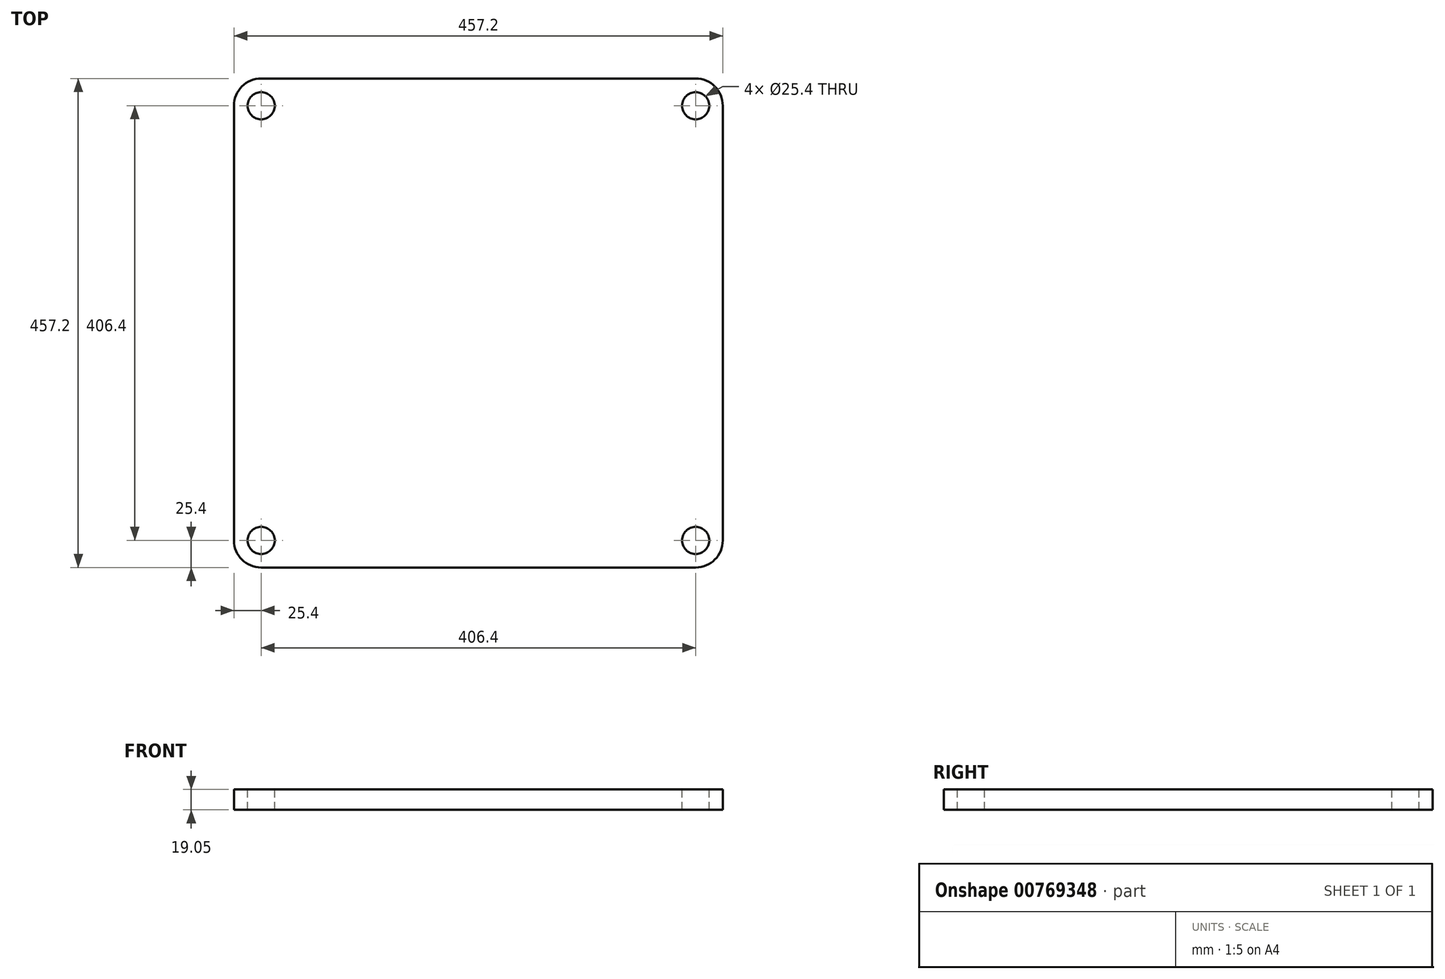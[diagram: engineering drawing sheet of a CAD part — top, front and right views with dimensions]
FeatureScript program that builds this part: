
annotation { "Feature Type Name" : "Feature", "Feature Type Description" : "" }
export const myFeature = defineFeature(function(context is Context, id is Id, definition is map)
    precondition{}
    {
        {
            var Q0;
            Q0=qCreatedBy(makeId("Top.planeOp"),FACE);
            var sketch = newSketch(context, id + "F0", { "sketchPlane" : qUnion([Q0])});
            skLineSegment(sketch, "E0.bottom", {"start": v(228.6, 228.6) * mm, "end": v(-228.6, 228.6) * mm});
            skLineSegment(sketch, "E0.top", {"start": v(228.6, -228.6) * mm, "end": v(-228.6, -228.6) * mm});
            skLineSegment(sketch, "E0.left", {"start": v(228.6, 228.6) * mm, "end": v(228.6, -228.6) * mm});
            skLineSegment(sketch, "E0.right", {"start": v(-228.6, 228.6) * mm, "end": v(-228.6, -228.6) * mm});
            skPoint(sketch, "E0.middle", {"position": v(0, 0) * mm});
            skSolve(sketch);
        }
        {
            var Q0;
            Q0=makeQuery(id+"F0.imprint","IMPRINT",FACE,{"disambiguationData":[TD([[makeQuery(id+"F0.imprint","IMPRINT",EDGE,{"derivedFrom":sQuery(id+"F0.wireOp",EDGE,"E0.bottom")}),1.0]])]});
            extrude(context, id + "F1", {"entities" : qUnion([Q0]), "depth" : 19.05 * mm, "offsetDistance" : 25.4 * mm});
        }
        {
            var Q0;
            Q0=makeQuery(id+"F1.opExtrude","SWEPT_EDGE",EDGE,{"disambiguationData":[OSD([sQuery(id+"F0.wireOp",EDGE,"E0.top"),sQuery(id+"F0.wireOp",EDGE,"E0.left")])]});
            var Q1;
            Q1=makeQuery(id+"F1.opExtrude","SWEPT_EDGE",EDGE,{"disambiguationData":[OSD([sQuery(id+"F0.wireOp",EDGE,"E0.bottom"),sQuery(id+"F0.wireOp",EDGE,"E0.left")])]});
            var Q2;
            Q2=makeQuery(id+"F1.opExtrude","SWEPT_EDGE",EDGE,{"disambiguationData":[OSD([sQuery(id+"F0.wireOp",EDGE,"E0.top"),sQuery(id+"F0.wireOp",EDGE,"E0.right")])]});
            var Q3;
            Q3=makeQuery(id+"F1.opExtrude","SWEPT_EDGE",EDGE,{"disambiguationData":[OSD([sQuery(id+"F0.wireOp",EDGE,"E0.bottom"),sQuery(id+"F0.wireOp",EDGE,"E0.right")])]});
            fillet(context, id + "F2", {"entities" : qUnion([Q0, Q1, Q2, Q3]), "radius" : 25.4 * mm, "tangentPropagation" : true, "allowEdgeOverflow" : false});
        }
        {
            var Q0;
            Q0=makeQuery(id+"F1.opExtrude","CAP_FACE",FACE,{"disambiguationData":[OSD([sQuery(id+"F0.wireOp",EDGE,"E0.bottom"),sQuery(id+"F0.wireOp",EDGE,"E0.top"),sQuery(id+"F0.wireOp",EDGE,"E0.left"),sQuery(id+"F0.wireOp",EDGE,"E0.right")])],"isStart":false});
            var sketch = newSketch(context, id + "F3", { "sketchPlane" : qUnion([Q0])});
            skArc(sketch, "E1.0", {"start": v(-203.2, 228.6) * mm, "mid": v(-221.16, 221.16) * mm, "end": v(-228.6, 203.2) * mm, "construction": true});
            skArc(sketch, "E2.0", {"start": v(228.6, 203.2) * mm, "mid": v(221.16, 221.16) * mm, "end": v(203.2, 228.6) * mm, "construction": true});
            skArc(sketch, "E3.0", {"start": v(203.2, -228.6) * mm, "mid": v(221.16, -221.16) * mm, "end": v(228.6, -203.2) * mm, "construction": true});
            skArc(sketch, "E4.0", {"start": v(-228.6, -203.2) * mm, "mid": v(-221.16, -221.16) * mm, "end": v(-203.2, -228.6) * mm, "construction": true});
            skCircle(sketch, "E5", {"center": v(-203.2, 203.2) * mm, "radius": 12.7 * mm});
            skCircle(sketch, "E6", {"center": v(203.2, 203.2) * mm, "radius": 12.7 * mm});
            skCircle(sketch, "E7", {"center": v(203.2, -203.2) * mm, "radius": 12.7 * mm});
            skCircle(sketch, "E8", {"center": v(-203.2, -203.2) * mm, "radius": 12.7 * mm});
            skSolve(sketch);
        }
        {
            var Q0;
            Q0=makeQuery(id+"F3.imprint","IMPRINT",FACE,{"disambiguationData":[TD([[makeQuery(id+"F3.imprint","IMPRINT",EDGE,{"derivedFrom":sQuery(id+"F3.wireOp",EDGE,"E5")}),1.0]])]});
            var Q1;
            Q1=makeQuery(id+"F3.imprint","IMPRINT",FACE,{"disambiguationData":[TD([[makeQuery(id+"F3.imprint","IMPRINT",EDGE,{"derivedFrom":sQuery(id+"F3.wireOp",EDGE,"E6")}),1.0]])]});
            var Q2;
            Q2=makeQuery(id+"F3.imprint","IMPRINT",FACE,{"disambiguationData":[TD([[makeQuery(id+"F3.imprint","IMPRINT",EDGE,{"derivedFrom":sQuery(id+"F3.wireOp",EDGE,"E7")}),1.0]])]});
            var Q3;
            Q3=makeQuery(id+"F3.imprint","IMPRINT",FACE,{"disambiguationData":[TD([[makeQuery(id+"F3.imprint","IMPRINT",EDGE,{"derivedFrom":sQuery(id+"F3.wireOp",EDGE,"E8")}),1.0]])]});
            var Q4;
            Q4=sQuery(id+"F3.wireOp",EDGE,"E5");
            var Q5;
            Q5=sQuery(id+"F3.wireOp",EDGE,"E6");
            var Q6;
            Q6=sQuery(id+"F3.wireOp",EDGE,"E7");
            var Q7;
            Q7=sQuery(id+"F3.wireOp",EDGE,"E8");
            extrude(context, id + "F4", {"entities" : qUnion([Q0, Q1, Q2, Q3]), "operationType" : NewBodyOperationType.REMOVE, "surfaceEntities" : qUnion([Q4, Q5, Q6, Q7]), "endBound" : BoundingType.UP_TO_NEXT, "oppositeDirection" : true, "depth" : 106.43 * mm, "offsetDistance" : 25.4 * mm});
        }
    });
